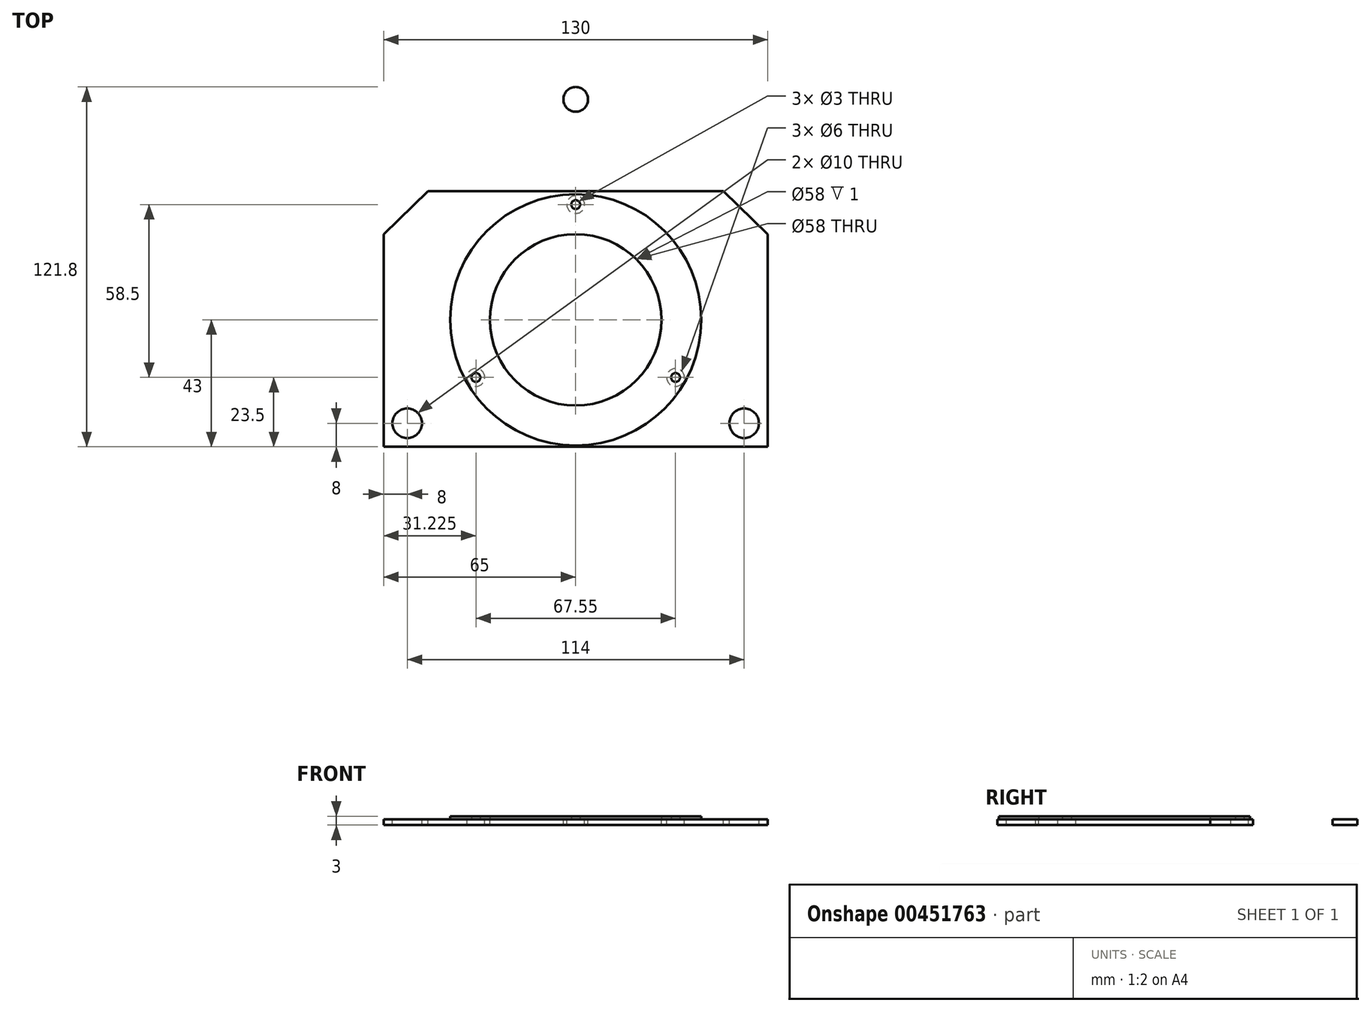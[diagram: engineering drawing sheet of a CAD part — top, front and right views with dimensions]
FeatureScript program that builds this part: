
annotation { "Feature Type Name" : "Feature", "Feature Type Description" : "" }
export const myFeature = defineFeature(function(context is Context, id is Id, definition is map)
    precondition{}
    {
        {
            var Q0;
            Q0=qCreatedBy(makeId("Top.planeOp"),FACE);
            var sketch = newSketch(context, id + "F0", { "sketchPlane" : qUnion([Q0])});
            skLineSegment(sketch, "E0", {"start": v(-65, -43) * mm, "end": v(65, -43) * mm});
            skLineSegment(sketch, "E1", {"start": v(65, -43) * mm, "end": v(65, 29) * mm});
            skLineSegment(sketch, "E2", {"start": v(65, 29) * mm, "end": v(50, 43.5) * mm});
            skLineSegment(sketch, "E3", {"start": v(50, 43.5) * mm, "end": v(-50, 43.5) * mm});
            skLineSegment(sketch, "E4", {"start": v(-50, 43.5) * mm, "end": v(-65, 29) * mm});
            skLineSegment(sketch, "E5", {"start": v(-65, 29) * mm, "end": v(-65, -43) * mm});
            skCircle(sketch, "E6", {"center": v(0, 0) * mm, "radius": 29 * mm});
            skCircle(sketch, "E7", {"center": v(0, 74.62) * mm, "radius": 4.18 * mm});
            skCircle(sketch, "E8", {"center": v(0, 0) * mm, "radius": 39 * mm, "construction": true});
            skCircle(sketch, "E9", {"center": v(0, 39) * mm, "radius": 3 * mm});
            skCircle(sketch, "E10.1.0", {"center": v(-33.77, -19.5) * mm, "radius": 3 * mm});
            skCircle(sketch, "E10.2.0", {"center": v(33.77, -19.5) * mm, "radius": 3 * mm});
            skCircle(sketch, "E11", {"center": v(-57, -35) * mm, "radius": 5 * mm});
            skCircle(sketch, "E12", {"center": v(57, -35) * mm, "radius": 5 * mm});
            skSolve(sketch);
        }
        {
            var Q0;
            Q0 = qSketchRegion(id + "F0", true);
            extrude(context, id + "F1", {"entities" : qUnion([Q0]), "oppositeDirection" : true, "depth" : 2 * mm});
        }
        {
            var Q0;
            Q0=makeQuery(id+"F1.opExtrude","CAP_FACE",FACE,{"disambiguationData":[OSD([sQuery(id+"F0.wireOp",EDGE,"E0"),sQuery(id+"F0.wireOp",EDGE,"E1"),sQuery(id+"F0.wireOp",EDGE,"E2"),sQuery(id+"F0.wireOp",EDGE,"E3"),sQuery(id+"F0.wireOp",EDGE,"E4"),sQuery(id+"F0.wireOp",EDGE,"E5"),sQuery(id+"F0.wireOp",EDGE,"E6"),sQuery(id+"F0.wireOp",EDGE,"E9"),sQuery(id+"F0.wireOp",EDGE,"E10.1.0"),sQuery(id+"F0.wireOp",EDGE,"E10.2.0"),sQuery(id+"F0.wireOp",EDGE,"E11"),sQuery(id+"F0.wireOp",EDGE,"E12")])],"isStart":true});
            var sketch = newSketch(context, id + "F2", { "sketchPlane" : qUnion([Q0])});
            skCircle(sketch, "E13", {"center": v(0, 0) * mm, "radius": 29 * mm});
            skCircle(sketch, "E14", {"center": v(0, 0) * mm, "radius": 42.5 * mm});
            skCircle(sketch, "E15", {"center": v(0, 0) * mm, "radius": 39 * mm, "construction": true});
            skCircle(sketch, "E16", {"center": v(0, 39) * mm, "radius": 1.5 * mm});
            skCircle(sketch, "E17.1.0", {"center": v(-33.77, -19.5) * mm, "radius": 1.5 * mm});
            skCircle(sketch, "E17.2.0", {"center": v(33.77, -19.5) * mm, "radius": 1.5 * mm});
            skSolve(sketch);
        }
        {
            var Q0;
            Q0 = qSketchRegion(id + "F2", true);
            extrude(context, id + "F3", {"entities" : qUnion([Q0]), "depth" : 1 * mm});
        }
    });
